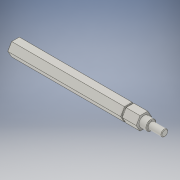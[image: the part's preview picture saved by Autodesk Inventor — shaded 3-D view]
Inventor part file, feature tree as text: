
AUTODESK INVENTOR PART (.ipt)
format: ipt  version: 2017.1 (Build 211199000, 199)  size: 126,464 bytes
history: native  units: in
note: dims shown in document units (in); Inventor stores cm internally (conversion verified against a paired STEP export)
features: chamfer x1
ambient origin geometry x8: Origin, YZ Plane, XZ Plane, XY Plane, X Axis, Y Axis, Z Axis, Center Point
bodies: Solid1 (feature_tree)
feature tree (1):
  chamfer  "Chamfer1"  [1 undecoded]
note: 1 required parameter value undecoded (feature->parameter linkage not recoverable at this tier; creation-order binding heuristic only, values carry confidence <= 0.55)
